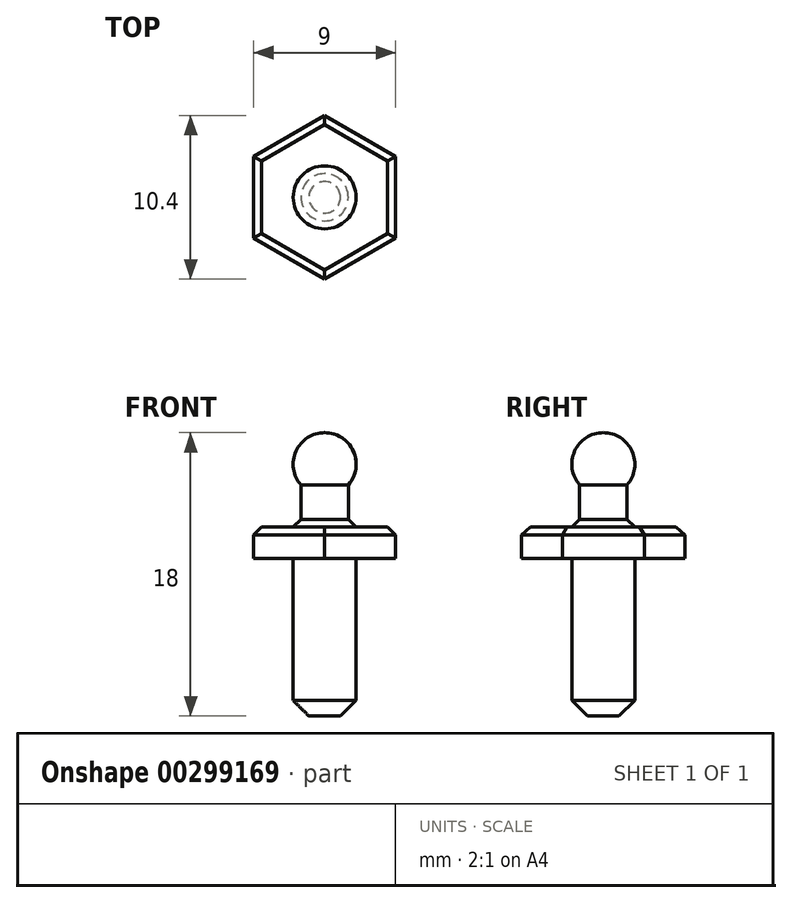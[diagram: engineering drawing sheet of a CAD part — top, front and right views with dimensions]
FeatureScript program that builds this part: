
annotation { "Feature Type Name" : "Feature", "Feature Type Description" : "" }
export const myFeature = defineFeature(function(context is Context, id is Id, definition is map)
    precondition{}
    {
        {
            var Q0;
            Q0=qCreatedBy(makeId("Top.planeOp"),FACE);
            var sketch = newSketch(context, id + "F0", { "sketchPlane" : qUnion([Q0])});
            skCircle(sketch, "E0.cCircle", {"center": v(0, 0) * mm, "radius": 4.5 * mm, "construction": true});
            skLineSegment(sketch, "E0.0", {"start": v(4.5, 2.6) * mm, "end": v(4.5, -2.6) * mm});
            skLineSegment(sketch, "E0.1", {"start": v(4.5, -2.6) * mm, "end": v(0, -5.2) * mm});
            skLineSegment(sketch, "E0.2", {"start": v(0, -5.2) * mm, "end": v(-4.5, -2.6) * mm});
            skLineSegment(sketch, "E0.3", {"start": v(-4.5, -2.6) * mm, "end": v(-4.5, 2.6) * mm});
            skLineSegment(sketch, "E0.4", {"start": v(-4.5, 2.6) * mm, "end": v(0, 5.2) * mm});
            skLineSegment(sketch, "E0.5", {"start": v(0, 5.2) * mm, "end": v(4.5, 2.6) * mm});
            skPoint(sketch, "E0.0.midPoint", {"position": v(4.5, 0) * mm});
            skSolve(sketch);
        }
        {
            var Q0;
            Q0 = qSketchRegion(id + "F0", true);
            extrude(context, id + "F1", {"entities" : qUnion([Q0]), "depth" : 2 * mm});
        }
        {
            var Q0;
            Q0=makeQuery(id+"F1.opExtrude","CAP_FACE",FACE,{"disambiguationData":[OSD([sQuery(id+"F0.wireOp",EDGE,"E0.0"),sQuery(id+"F0.wireOp",EDGE,"E0.1"),sQuery(id+"F0.wireOp",EDGE,"E0.2"),sQuery(id+"F0.wireOp",EDGE,"E0.3"),sQuery(id+"F0.wireOp",EDGE,"E0.4"),sQuery(id+"F0.wireOp",EDGE,"E0.5")])],"isStart":true});
            var sketch = newSketch(context, id + "F2", { "sketchPlane" : qUnion([Q0])});
            skCircle(sketch, "E1", {"center": v(0, 0) * mm, "radius": 2 * mm});
            skSolve(sketch);
        }
        {
            var Q0;
            Q0 = qSketchRegion(id + "F2", true);
            extrude(context, id + "F3", {"entities" : qUnion([Q0]), "operationType" : NewBodyOperationType.ADD, "depth" : 10 * mm});
        }
        {
            var Q0;
            Q0=makeQuery(id+"F3.opExtrude","CAP_EDGE",EDGE,{"disambiguationData":[OSD([sQuery(id+"F2.wireOp",EDGE,"E1")])],"isStart":false});
            chamfer(context, id + "F4", {"entities" : qUnion([Q0]), "width" : 1 * mm, "tangentPropagation" : true});
        }
        {
            var Q0;
            Q0=makeQuery(id+"F1.opExtrude","CAP_FACE",FACE,{"disambiguationData":[OSD([sQuery(id+"F0.wireOp",EDGE,"E0.0"),sQuery(id+"F0.wireOp",EDGE,"E0.1"),sQuery(id+"F0.wireOp",EDGE,"E0.2"),sQuery(id+"F0.wireOp",EDGE,"E0.3"),sQuery(id+"F0.wireOp",EDGE,"E0.4"),sQuery(id+"F0.wireOp",EDGE,"E0.5")])],"isStart":false});
            var sketch = newSketch(context, id + "F5", { "sketchPlane" : qUnion([Q0])});
            skCircle(sketch, "E2", {"center": v(0, 0) * mm, "radius": 1.5 * mm});
            skSolve(sketch);
        }
        {
            var Q0;
            Q0 = qSketchRegion(id + "F5", true);
            extrude(context, id + "F6", {"entities" : qUnion([Q0]), "operationType" : NewBodyOperationType.ADD, "depth" : 3 * mm});
        }
        {
            var Q0;
            Q0=qCreatedBy(makeId("Front.planeOp"),FACE);
            var sketch = newSketch(context, id + "F7", { "sketchPlane" : qUnion([Q0])});
            skArc(sketch, "E3", {"start": v(1.5, 4.68) * mm, "mid": v(1.82, 6.82) * mm, "end": v(0, 8) * mm});
            skLineSegment(sketch, "E4", {"start": v(0, 0) * mm, "end": v(0, 4) * mm, "construction": true});
            skLineSegment(sketch, "E5", {"start": v(0, 8) * mm, "end": v(0, 4) * mm});
            skLineSegment(sketch, "E6.0", {"start": v(-1.5, 5) * mm, "end": v(1.5, 5) * mm});
            skLineSegment(sketch, "E7", {"start": v(1.5, 5) * mm, "end": v(1.5, 4.68) * mm});
            skLineSegment(sketch, "E8.trimOffspring", {"start": v(0, 5) * mm, "end": v(0, 9.56) * mm, "construction": true});
            skSolve(sketch);
        }
        {
            var Q0;
            Q0=makeQuery(id+"F7.imprint","IMPRINT",FACE,{"disambiguationData":[TD([[makeQuery(id+"F7.imprint","IMPRINT",EDGE,{"derivedFrom":sQuery(id+"F7.wireOp",EDGE,"E3")}),1.0]])]});
            var Q1;
            Q1=sQuery(id+"F7.wireOp",EDGE,"E4");
            revolve(context, id + "F8", {"operationType" : NewBodyOperationType.ADD, "entities" : qUnion([Q0]), "axis" : qUnion([Q1]), "revolveType" : RevolveType.FULL, "oppositeDirection" : true});
        }
        {
            var Q0;
            Q0=makeQuery(id+"F1.opExtrude","CAP_EDGE",EDGE,{"disambiguationData":[OSD([sQuery(id+"F0.wireOp",EDGE,"E0.1")])],"isStart":false});
            var Q1;
            Q1=makeQuery(id+"F1.opExtrude","CAP_EDGE",EDGE,{"disambiguationData":[OSD([sQuery(id+"F0.wireOp",EDGE,"E0.0")])],"isStart":false});
            var Q2;
            Q2=makeQuery(id+"F1.opExtrude","CAP_EDGE",EDGE,{"disambiguationData":[OSD([sQuery(id+"F0.wireOp",EDGE,"E0.5")])],"isStart":false});
            var Q3;
            Q3=makeQuery(id+"F1.opExtrude","CAP_EDGE",EDGE,{"disambiguationData":[OSD([sQuery(id+"F0.wireOp",EDGE,"E0.4")])],"isStart":false});
            var Q4;
            Q4=makeQuery(id+"F1.opExtrude","CAP_FACE",FACE,{"disambiguationData":[OSD([sQuery(id+"F0.wireOp",EDGE,"E0.0"),sQuery(id+"F0.wireOp",EDGE,"E0.1"),sQuery(id+"F0.wireOp",EDGE,"E0.2"),sQuery(id+"F0.wireOp",EDGE,"E0.3"),sQuery(id+"F0.wireOp",EDGE,"E0.4"),sQuery(id+"F0.wireOp",EDGE,"E0.5")])],"isStart":false});
            chamfer(context, id + "F9", {"entities" : qUnion([Q0, Q1, Q2, Q3, Q4]), "width" : 0.5 * mm, "tangentPropagation" : true});
        }
    });
